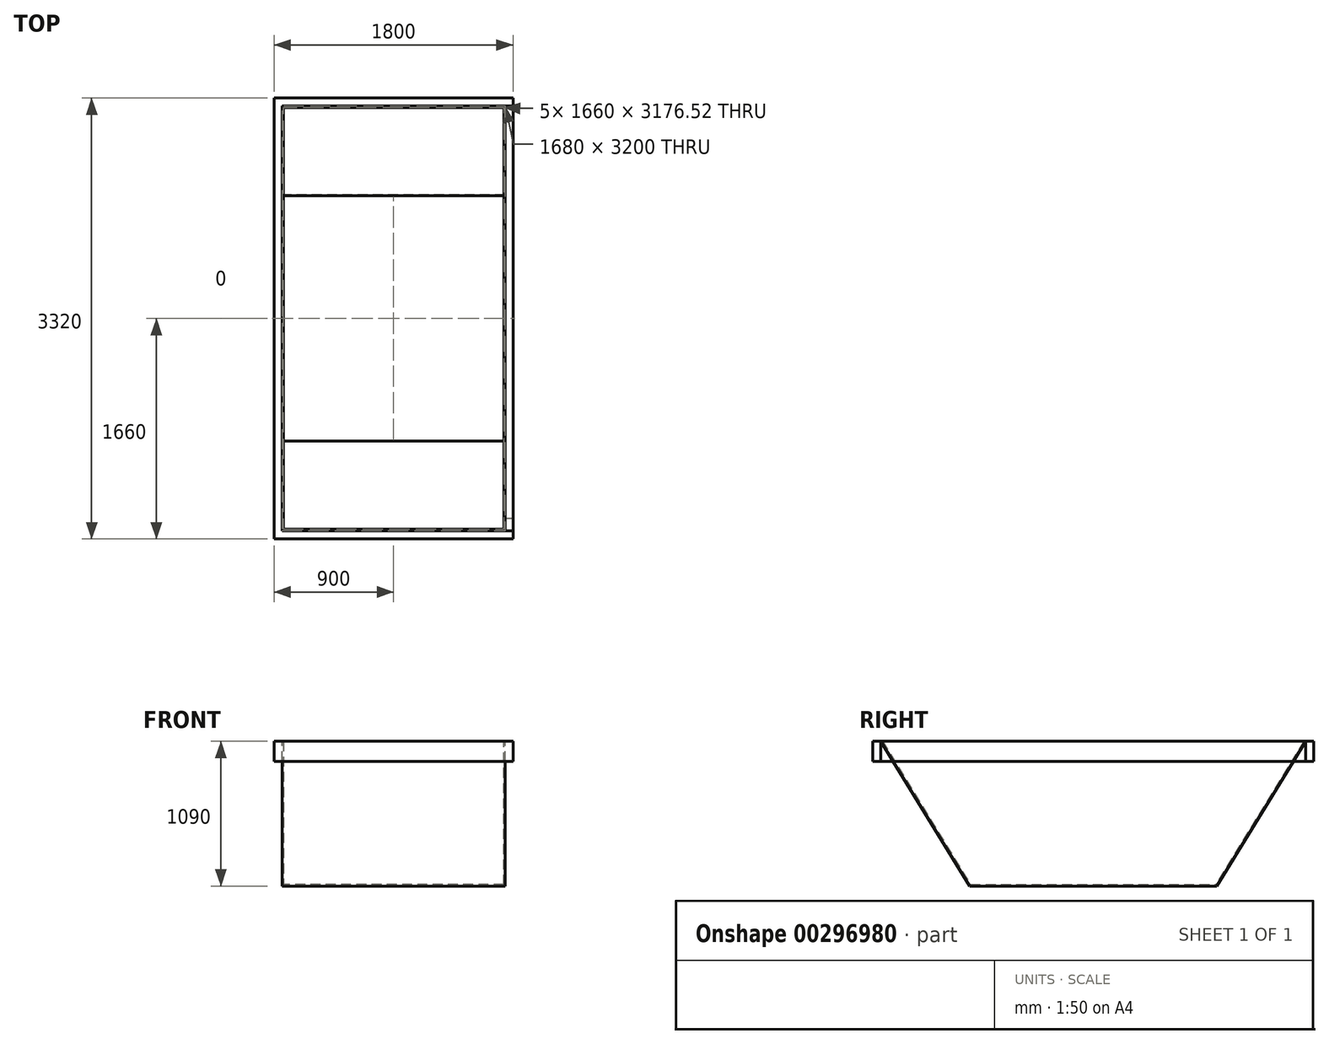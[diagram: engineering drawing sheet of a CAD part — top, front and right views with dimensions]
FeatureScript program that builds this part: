
annotation { "Feature Type Name" : "Feature", "Feature Type Description" : "" }
export const myFeature = defineFeature(function(context is Context, id is Id, definition is map)
    precondition{}
    {
        {
            var Q0;
            Q0=qCreatedBy(makeId("Top.planeOp"),FACE);
            var sketch = newSketch(context, id + "F0", { "sketchPlane" : qUnion([Q0])});
            skLineSegment(sketch, "E0.bottom", {"start": v(900, -1660) * mm, "end": v(-900, -1660) * mm});
            skLineSegment(sketch, "E0.top", {"start": v(900, 1660) * mm, "end": v(-900, 1660) * mm});
            skLineSegment(sketch, "E0.left", {"start": v(900, -1660) * mm, "end": v(900, 1660) * mm});
            skLineSegment(sketch, "E0.right", {"start": v(-900, -1660) * mm, "end": v(-900, 1660) * mm});
            skPoint(sketch, "E0.middle", {"position": v(0, 0) * mm});
            skLineSegment(sketch, "E1.bottom", {"start": v(840, -1600) * mm, "end": v(-840, -1600) * mm});
            skLineSegment(sketch, "E1.top", {"start": v(840, 1600) * mm, "end": v(-840, 1600) * mm});
            skLineSegment(sketch, "E1.left", {"start": v(840, -1600) * mm, "end": v(840, 1600) * mm});
            skLineSegment(sketch, "E1.right", {"start": v(-840, -1600) * mm, "end": v(-840, 1600) * mm});
            skSolve(sketch);
        }
        {
            var Q0;
            Q0=makeQuery(id+"F0.imprint","IMPRINT",FACE,{"disambiguationData":[TD([[makeQuery(id+"F0.imprint","IMPRINT",EDGE,{"derivedFrom":sQuery(id+"F0.wireOp",EDGE,"E1.bottom")}),-1.0]])]});
            extrude(context, id + "F1", {"entities" : qUnion([Q0]), "oppositeDirection" : true, "depth" : 1090 * mm});
        }
        {
            var Q0;
            Q0=makeQuery(id+"F1.opExtrude","SWEPT_FACE",FACE,{"disambiguationData":[OSD([sQuery(id+"F0.wireOp",EDGE,"E1.right")])]});
            var sketch = newSketch(context, id + "F2", { "sketchPlane" : qUnion([Q0])});
            skLineSegment(sketch, "E2", {"start": v(-1600, 0) * mm, "end": v(-930, -1090) * mm});
            skLineSegment(sketch, "E3", {"start": v(1600, 0) * mm, "end": v(930, -1090) * mm});
            skSolve(sketch);
        }
        {
            var Q0;
            {var subQ0=sQuery(id+"F2.wireOp",EDGE,"E2");Q0=makeQuery(id+"F2.imprint","IMPRINT",FACE,{"disambiguationData":[TD([[makeQuery(id+"F2.imprint","IMPRINT",EDGE,{"derivedFrom":subQ0}),-1.0]])]});}
            var Q1;
            {var subQ0=sQuery(id+"F2.wireOp",EDGE,"E3");Q1=makeQuery(id+"F2.imprint","IMPRINT",FACE,{"disambiguationData":[TD([[makeQuery(id+"F2.imprint","IMPRINT",EDGE,{"derivedFrom":subQ0}),1.0]])]});}
            extrude(context, id + "F3", {"entities" : qUnion([Q0, Q1]), "operationType" : NewBodyOperationType.REMOVE, "endBound" : BoundingType.THROUGH_ALL, "oppositeDirection" : true, "depth" : 25 * mm});
        }
        {
            var Q0;
            Q0=makeQuery(id+"F1.opExtrude","CAP_FACE",FACE,{"disambiguationData":[OSD([sQuery(id+"F0.wireOp",EDGE,"E1.bottom"),sQuery(id+"F0.wireOp",EDGE,"E1.top"),sQuery(id+"F0.wireOp",EDGE,"E1.left"),sQuery(id+"F0.wireOp",EDGE,"E1.right")])],"isStart":true});
            shell(context, id + "F4", {"entities" : qUnion([Q0]), "thickness" : 10 * mm});
        }
        {
            var Q0;
            Q0=makeQuery(id+"F0.imprint","IMPRINT",FACE,{"disambiguationData":[TD([[makeQuery(id+"F0.imprint","IMPRINT",EDGE,{"derivedFrom":sQuery(id+"F0.wireOp",EDGE,"E0.bottom")}),-1.0]])]});
            extrude(context, id + "F5", {"entities" : qUnion([Q0]), "oppositeDirection" : true, "depth" : 150 * mm});
        }
    });
